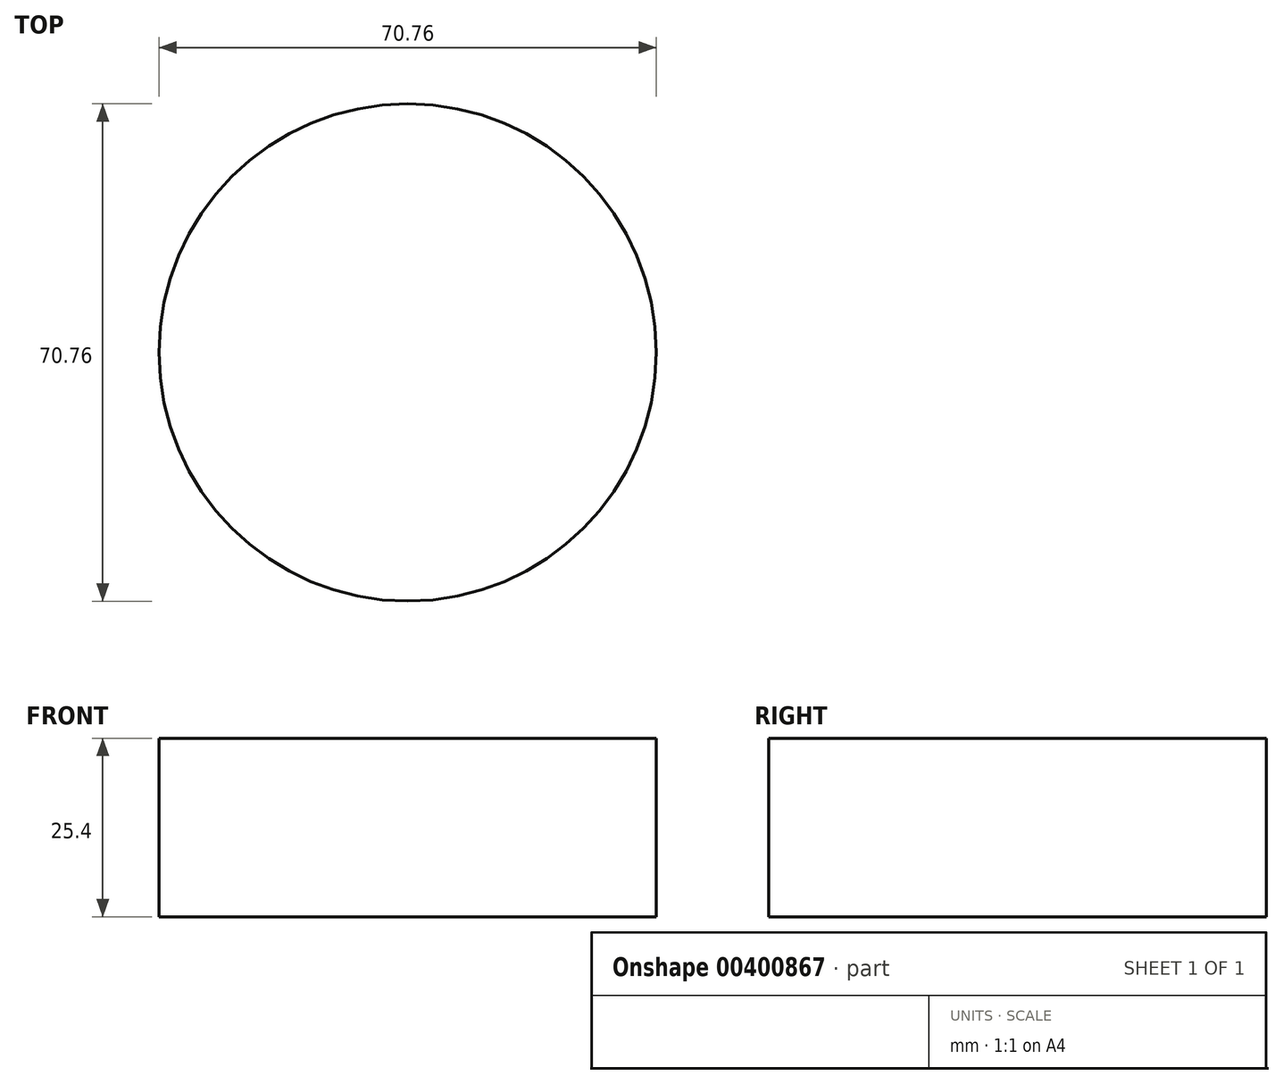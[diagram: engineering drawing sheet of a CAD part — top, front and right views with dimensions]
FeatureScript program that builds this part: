
annotation { "Feature Type Name" : "Feature", "Feature Type Description" : "" }
export const myFeature = defineFeature(function(context is Context, id is Id, definition is map)
    precondition{}
    {
        {
            var Q0;
            Q0=qCreatedBy(makeId("Top.planeOp"),FACE);
            var sketch = newSketch(context, id + "F0", { "sketchPlane" : qUnion([Q0])});
            skCircle(sketch, "E0", {"center": v(0, 0) * mm, "radius": 35.38 * mm});
            skSolve(sketch);
        }
        {
            var Q0;
            Q0=makeQuery(id+"F0.imprint","IMPRINT",FACE,{"disambiguationData":[TD([[makeQuery(id+"F0.imprint","IMPRINT",EDGE,{"derivedFrom":sQuery(id+"F0.wireOp",EDGE,"E0")}),1.0]])]});
            extrude(context, id + "F1", {"entities" : qUnion([Q0]), "depth" : 25.4 * mm});
        }
    });
